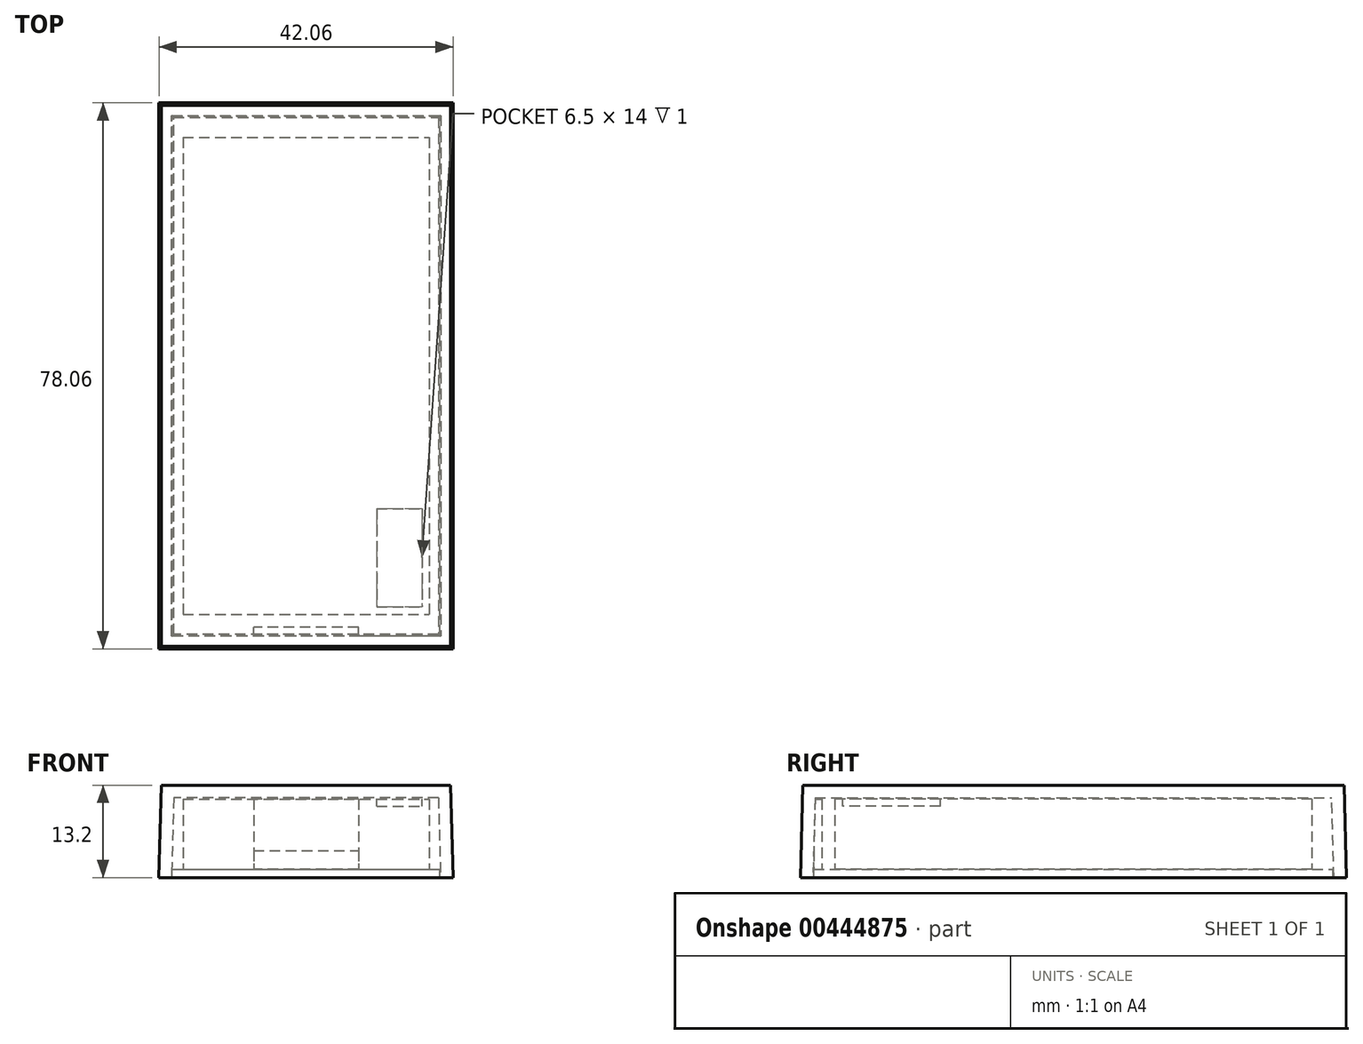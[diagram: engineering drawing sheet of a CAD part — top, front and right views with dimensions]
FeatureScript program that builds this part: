
annotation { "Feature Type Name" : "Feature", "Feature Type Description" : "" }
export const myFeature = defineFeature(function(context is Context, id is Id, definition is map)
    precondition{}
    {
        {
            var Q0;
            Q0=qCreatedBy(makeId("Top.planeOp"),FACE);
            var sketch = newSketch(context, id + "F0", { "sketchPlane" : qUnion([Q0])});
            skLineSegment(sketch, "E0.bottom", {"start": v(-17.6, 34.1) * mm, "end": v(17.6, 34.1) * mm});
            skLineSegment(sketch, "E0.top", {"start": v(-17.6, -34.1) * mm, "end": v(17.6, -34.1) * mm});
            skLineSegment(sketch, "E0.left", {"start": v(-17.6, 34.1) * mm, "end": v(-17.6, -34.1) * mm});
            skLineSegment(sketch, "E0.right", {"start": v(17.6, 34.1) * mm, "end": v(17.6, -34.1) * mm});
            skPoint(sketch, "E0.middle", {"position": v(0, 0) * mm});
            skSolve(sketch);
        }
        {
            var Q0;
            Q0 = qSketchRegion(id + "F0", true);
            extrude(context, id + "F1", {"entities" : qUnion([Q0]), "depth" : 10 * mm});
        }
        {
            var Q0;
            Q0=makeQuery(id+"F1.opExtrude","CAP_FACE",FACE,{"disambiguationData":[OSD([sQuery(id+"F0.wireOp",EDGE,"E0.bottom"),sQuery(id+"F0.wireOp",EDGE,"E0.top"),sQuery(id+"F0.wireOp",EDGE,"E0.left"),sQuery(id+"F0.wireOp",EDGE,"E0.right")])],"isStart":false});
            var sketch = newSketch(context, id + "F2", { "sketchPlane" : qUnion([Q0])});
            skLineSegment(sketch, "E1.bottom", {"start": v(10.1, -19) * mm, "end": v(16.6, -19) * mm});
            skLineSegment(sketch, "E1.top", {"start": v(10.1, -33) * mm, "end": v(16.6, -33) * mm});
            skLineSegment(sketch, "E1.left", {"start": v(10.1, -19) * mm, "end": v(10.1, -33) * mm});
            skLineSegment(sketch, "E1.right", {"start": v(16.6, -19) * mm, "end": v(16.6, -33) * mm});
            skSolve(sketch);
        }
        {
            var Q0;
            Q0 = qSketchRegion(id + "F2", true);
            extrude(context, id + "F3", {"entities" : qUnion([Q0]), "operationType" : NewBodyOperationType.REMOVE, "oppositeDirection" : true, "depth" : 1 * mm});
        }
        {
            var Q0;
            Q0=makeQuery(id+"F1.opExtrude","CAP_FACE",FACE,{"disambiguationData":[OSD([sQuery(id+"F0.wireOp",EDGE,"E0.bottom"),sQuery(id+"F0.wireOp",EDGE,"E0.top"),sQuery(id+"F0.wireOp",EDGE,"E0.left"),sQuery(id+"F0.wireOp",EDGE,"E0.right")])],"isStart":true});
            var sketch = newSketch(context, id + "F4", { "sketchPlane" : qUnion([Q0])});
            skSolve(sketch);
        }
        {
            var Q0;
            Q0=makeQuery(id+"F4.imprint","IMPRINT",FACE,{"disambiguationData":[TD([[makeQuery(id+"F4.imprint","IMPRINT",EDGE,{"derivedFrom":makeQuery(id+"F1.opExtrude","CAP_EDGE",EDGE,{"disambiguationData":[OSD([sQuery(id+"F0.wireOp",EDGE,"E0.bottom")])],"isStart":true})}),1.0]])]});
            var sketch = newSketch(context, id + "F5", { "sketchPlane" : qUnion([Q0])});
            skLineSegment(sketch, "E2.bottom", {"start": v(-21, 39) * mm, "end": v(21, 39) * mm});
            skLineSegment(sketch, "E2.top", {"start": v(-21, -39) * mm, "end": v(21, -39) * mm});
            skLineSegment(sketch, "E2.left", {"start": v(-21, 39) * mm, "end": v(-21, -39) * mm});
            skLineSegment(sketch, "E2.right", {"start": v(21, 39) * mm, "end": v(21, -39) * mm});
            skPoint(sketch, "E2.middle", {"position": v(0, 0) * mm});
            skSolve(sketch);
        }
        {
            var Q0;
            Q0 = qSketchRegion(id + "F5", true);
            extrude(context, id + "F6", {"entities" : qUnion([Q0]), "oppositeDirection" : true, "depth" : 12 * mm, "hasDraft" : true, "draftAngle" : 1.5 * degree, "draftPullDirection" : true, "hasSecondDirection" : true, "secondDirectionOppositeDirection" : false, "secondDirectionDepth" : 1.2 * mm, "hasSecondDirectionDraft" : true, "secondDirectionDraftAngle" : 1.5 * degree});
        }
        {
            var Q0;
            Q0=makeQuery(id+"F6.opExtrude","CAP_FACE",FACE,{"disambiguationData":[OSD([sQuery(id+"F5.wireOp",EDGE,"E2.bottom"),sQuery(id+"F5.wireOp",EDGE,"E2.top"),sQuery(id+"F5.wireOp",EDGE,"E2.left"),sQuery(id+"F5.wireOp",EDGE,"E2.right")])],"isStart":true});
            shell(context, id + "F7", {"entities" : qUnion([Q0]), "thickness" : 1.8 * mm});
        }
        {
            var Q0;
            Q0=makeQuery(id+"F4.imprint","IMPRINT",FACE,{"disambiguationData":[TD([[makeQuery(id+"F4.imprint","IMPRINT",EDGE,{"derivedFrom":makeQuery(id+"F1.opExtrude","CAP_EDGE",EDGE,{"disambiguationData":[OSD([sQuery(id+"F0.wireOp",EDGE,"E0.bottom")])],"isStart":true})}),1.0]])]});
            var sketch = newSketch(context, id + "F8", { "sketchPlane" : qUnion([Q0])});
            skLineSegment(sketch, "E3.bottom", {"start": v(-19.13, 37.13) * mm, "end": v(19.13, 37.13) * mm});
            skLineSegment(sketch, "E3.top", {"start": v(-19.13, -37.13) * mm, "end": v(19.13, -37.13) * mm});
            skLineSegment(sketch, "E3.left", {"start": v(-19.13, 37.13) * mm, "end": v(-19.13, -37.13) * mm});
            skLineSegment(sketch, "E3.right", {"start": v(19.13, 37.13) * mm, "end": v(19.13, -37.13) * mm});
            skPoint(sketch, "E3.middle", {"position": v(0, 0) * mm});
            skSolve(sketch);
        }
        {
            var Q0;
            Q0 = qSketchRegion(id + "F8", true);
            extrude(context, id + "F9", {"entities" : qUnion([Q0]), "depth" : 1.2 * mm});
        }
        {
            var Q0;
            Q0=makeQuery(id+"F9.opExtrude","CAP_FACE",FACE,{"disambiguationData":[OSD([sQuery(id+"F8.wireOp",EDGE,"E3.bottom"),sQuery(id+"F8.wireOp",EDGE,"E3.top"),sQuery(id+"F8.wireOp",EDGE,"E3.left"),sQuery(id+"F8.wireOp",EDGE,"E3.right")])],"isStart":true});
            var sketch = newSketch(context, id + "F10", { "sketchPlane" : qUnion([Q0])});
            skLineSegment(sketch, "E4.bottom", {"start": v(7.5, -37.13) * mm, "end": v(-7.5, -37.13) * mm});
            skLineSegment(sketch, "E4.top", {"start": v(7.5, -35.93) * mm, "end": v(-7.5, -35.93) * mm});
            skLineSegment(sketch, "E4.left", {"start": v(7.5, -37.13) * mm, "end": v(7.5, -35.93) * mm});
            skLineSegment(sketch, "E4.right", {"start": v(-7.5, -37.13) * mm, "end": v(-7.5, -35.93) * mm});
            skPoint(sketch, "E4.middle", {"position": v(0, -36.53) * mm});
            skPoint(sketch, "E4.middle.positionSnap0", {"position": v(0, -37.13) * mm});
            skPoint(sketch, "E4.centerSnap0", {"position": v(0, -37.13) * mm});
            skSolve(sketch);
        }
        {
            var Q0;
            Q0 = qSketchRegion(id + "F10", true);
            extrude(context, id + "F11", {"entities" : qUnion([Q0]), "operationType" : NewBodyOperationType.ADD, "depth" : 10 * mm});
        }
        {
            var Q0;
            Q0=makeQuery(id+"F11.opExtrude","SWEPT_FACE",FACE,{"disambiguationData":[OSD([sQuery(id+"F10.wireOp",EDGE,"E4.right")])]});
            var sketch = newSketch(context, id + "F12", { "sketchPlane" : qUnion([Q0])});
            skLineSegment(sketch, "E5", {"start": v(37.13, 5.4) * mm, "end": v(37.93, 5.4) * mm});
            skLineSegment(sketch, "E6", {"start": v(37.93, 5.4) * mm, "end": v(37.13, 7) * mm});
            skLineSegment(sketch, "E7", {"start": v(37.13, 7) * mm, "end": v(37.13, 5.4) * mm});
            skSolve(sketch);
        }
        {
            var Q0;
            Q0 = qSketchRegion(id + "F12", true);
            var Q1;
            Q1=makeQuery(id+"F11.opExtrude","SWEPT_FACE",FACE,{"disambiguationData":[OSD([sQuery(id+"F10.wireOp",EDGE,"E4.left")])]});
            extrude(context, id + "F13", {"entities" : qUnion([Q0]), "operationType" : NewBodyOperationType.ADD, "endBound" : BoundingType.UP_TO_SURFACE, "oppositeDirection" : true, "endBoundEntityFace" : qUnion([Q1]), "depth" : 25 * mm});
        }
    });
